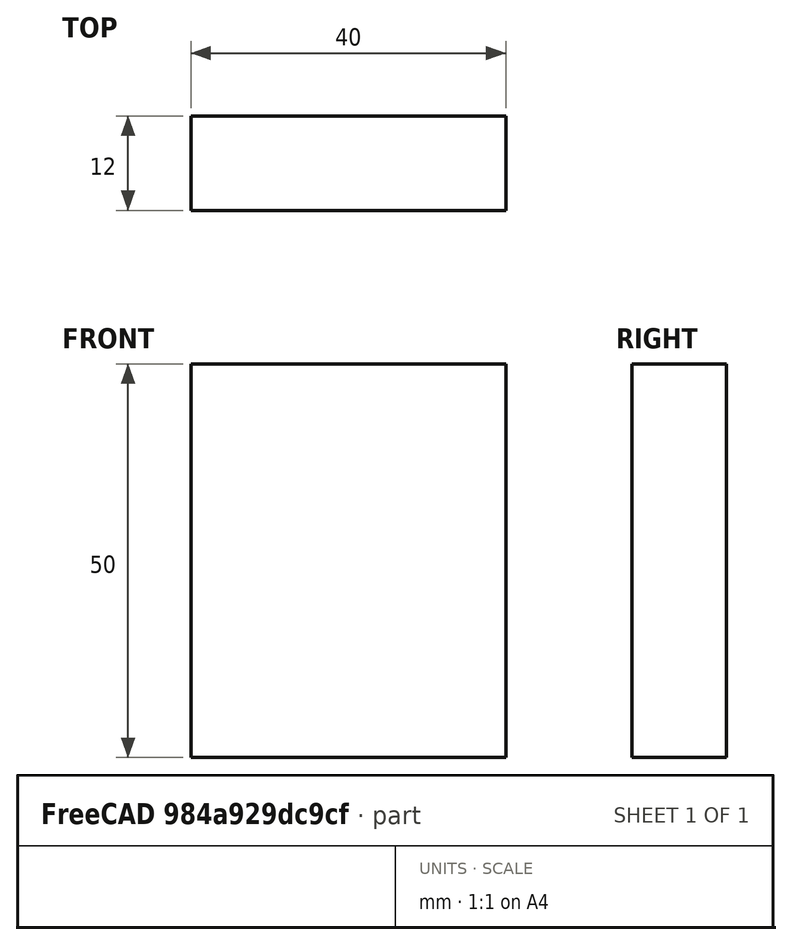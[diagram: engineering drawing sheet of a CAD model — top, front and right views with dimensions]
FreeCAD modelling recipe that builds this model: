
FCSTD DOCUMENT  (FreeCAD 0.15R4671 (Git))
Label: Flat Bar 40x12 EN10058 S235JR
License: All rights reserved
LicenseURL: http://en.wikipedia.org/wiki/All_rights_reserved
objects: Sketcher::SketchObject×1, Part::Extrusion×1
note: 2 computed .brp shape members not serialized (recipe doc carries the construction recipe); baked Part::Feature solids carry a one-line shape summary decoded from their .brp

FEATURE [Sketcher::SketchObject] Sketch
  sketch-geometry (4):
    g0: LineSegment StartX=-20 StartY=-6 StartZ=0 EndX=20 EndY=-6 EndZ=0
    g1: LineSegment StartX=20 StartY=-6 StartZ=0 EndX=20 EndY=6 EndZ=0
    g2: LineSegment StartX=20 StartY=6 StartZ=0 EndX=-20 EndY=6 EndZ=0
    g3: LineSegment StartX=-20 StartY=6 StartZ=0 EndX=-20 EndY=-6 EndZ=0
  constraints (12):
    c: Coincident(g0,g1)
    c: Coincident(g1,g2)
    c: Coincident(g2,g3)
    c: Coincident(g3,g0)
    c: Horizontal(g0)
    c: Horizontal(g2)
    c: Vertical(g1)
    c: Vertical(g3)
    c: Symmetric(g1,g2,g-2)
    c: Symmetric(g0,g1,g-1)
    c: DistanceY(g1) = 12
    c: DistanceX(g0) = 40
FEATURE [Part::Extrusion] Extrude  label="Flat Bar 40x12 EN10058 S235JR"
  Base = -> Sketch
  Dir = (0,0,50)
  Solid = true
